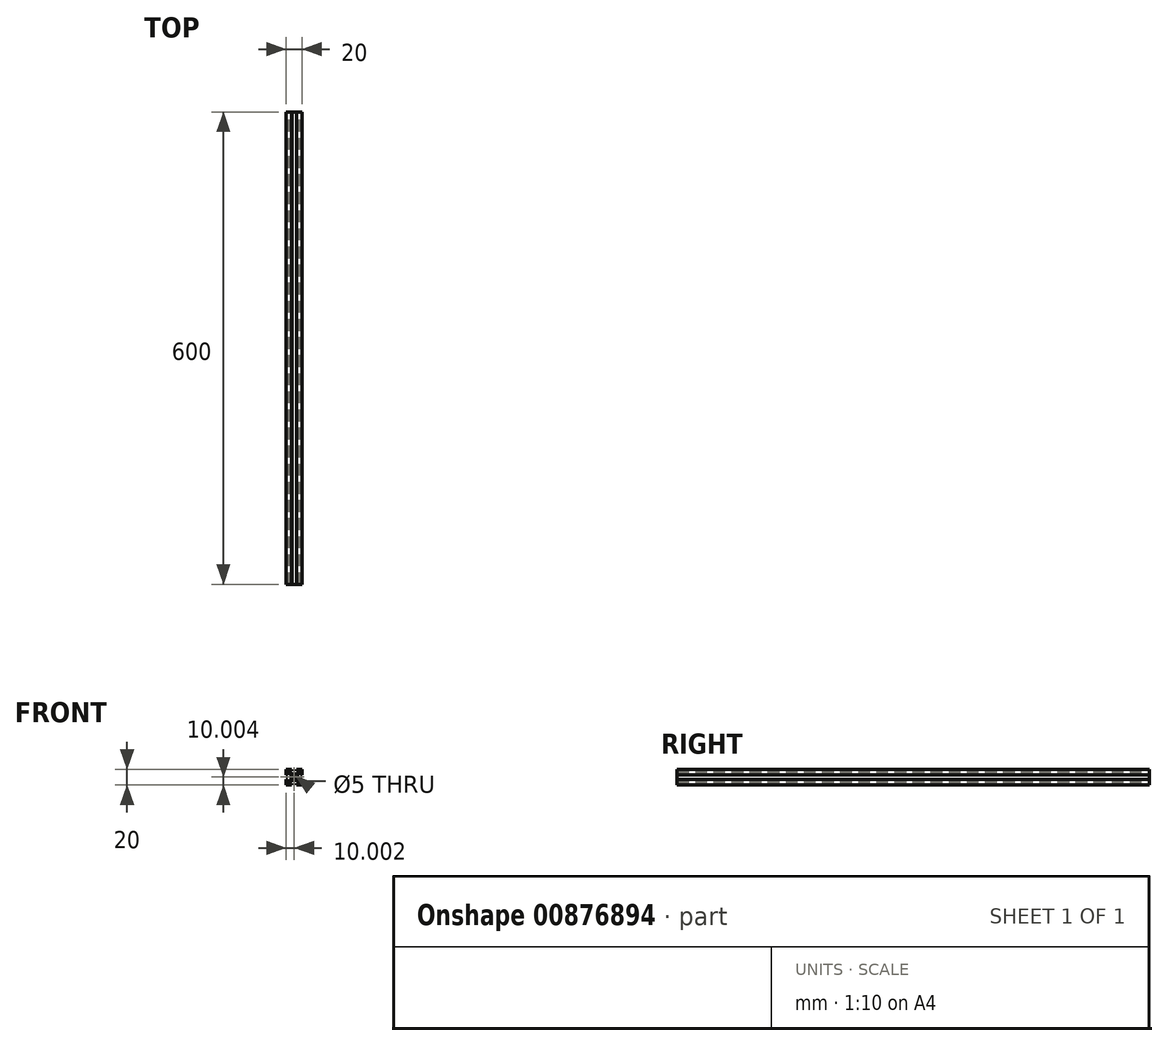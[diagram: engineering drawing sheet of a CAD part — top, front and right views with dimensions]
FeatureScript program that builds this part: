
annotation { "Feature Type Name" : "Feature", "Feature Type Description" : "" }
export const myFeature = defineFeature(function(context is Context, id is Id, definition is map)
    precondition{}
    {
        {
            var Q0;
            Q0=qCreatedBy(makeId("Front.planeOp"),FACE);
            var sketch = newSketch(context, id + "F0", { "sketchPlane" : qUnion([Q0])});
            skLineSegment(sketch, "E0.bottom", {"start": v(-32.56, 59.93) * mm, "end": v(-12.56, 59.93) * mm});
            skLineSegment(sketch, "E0.top", {"start": v(-32.56, 39.93) * mm, "end": v(-12.56, 39.93) * mm});
            skLineSegment(sketch, "E0.left", {"start": v(-32.56, 59.93) * mm, "end": v(-32.56, 39.93) * mm});
            skLineSegment(sketch, "E0.right", {"start": v(-12.56, 59.93) * mm, "end": v(-12.56, 39.93) * mm});
            skPoint(sketch, "E0.middle", {"position": v(-22.56, 49.93) * mm});
            skLineSegment(sketch, "E1", {"start": v(-14.36, 53.03) * mm, "end": v(-12.56, 53.03) * mm});
            skLineSegment(sketch, "E2.MirrorCS", {"start": v(-14.36, 46.83) * mm, "end": v(-12.56, 46.83) * mm});
            skLineSegment(sketch, "E3", {"start": v(-14.36, 53.03) * mm, "end": v(-14.36, 55.43) * mm});
            skLineSegment(sketch, "E4.MirrorCS", {"start": v(-14.36, 46.83) * mm, "end": v(-14.36, 44.43) * mm});
            skLineSegment(sketch, "E5", {"start": v(-14.36, 55.43) * mm, "end": v(-15.96, 55.43) * mm});
            skLineSegment(sketch, "E6.MirrorCS", {"start": v(-14.36, 44.43) * mm, "end": v(-15.96, 44.43) * mm});
            skCircle(sketch, "E7", {"center": v(-22.56, 49.93) * mm, "radius": 2.5 * mm});
            skLineSegment(sketch, "E8", {"start": v(-18.46, 52.93) * mm, "end": v(-18.46, 46.93) * mm});
            skLineSegment(sketch, "E9", {"start": v(-18.46, 52.93) * mm, "end": v(-15.96, 55.43) * mm});
            skLineSegment(sketch, "E10.MirrorCS", {"start": v(-18.46, 46.93) * mm, "end": v(-15.96, 44.43) * mm});
            skLineSegment(sketch, "E11.MirrorCS", {"start": v(-30.76, 53.03) * mm, "end": v(-32.56, 53.03) * mm});
            skLineSegment(sketch, "E12.MirrorCS", {"start": v(-30.76, 53.03) * mm, "end": v(-30.76, 55.43) * mm});
            skLineSegment(sketch, "E13.MirrorCS", {"start": v(-30.76, 55.43) * mm, "end": v(-29.16, 55.43) * mm});
            skLineSegment(sketch, "E14.MirrorCS", {"start": v(-26.66, 52.93) * mm, "end": v(-29.16, 55.43) * mm});
            skLineSegment(sketch, "E15.MirrorCS", {"start": v(-26.66, 52.93) * mm, "end": v(-26.66, 46.93) * mm});
            skLineSegment(sketch, "E16.MirrorCS", {"start": v(-26.66, 46.93) * mm, "end": v(-29.16, 44.43) * mm});
            skLineSegment(sketch, "E17.MirrorCS", {"start": v(-30.76, 44.43) * mm, "end": v(-29.16, 44.43) * mm});
            skLineSegment(sketch, "E18.MirrorCS", {"start": v(-30.76, 46.83) * mm, "end": v(-30.76, 44.43) * mm});
            skLineSegment(sketch, "E19.MirrorCS", {"start": v(-30.76, 46.83) * mm, "end": v(-32.56, 46.83) * mm});
            skLineSegment(sketch, "E20", {"start": v(-25.66, 59.93) * mm, "end": v(-25.66, 58.13) * mm});
            skLineSegment(sketch, "E21", {"start": v(-25.66, 58.13) * mm, "end": v(-28.06, 58.13) * mm});
            skLineSegment(sketch, "E22", {"start": v(-28.06, 58.13) * mm, "end": v(-28.06, 56.53) * mm});
            skLineSegment(sketch, "E23", {"start": v(-25.56, 54.03) * mm, "end": v(-22.56, 54.03) * mm});
            skLineSegment(sketch, "E24.MirrorCS", {"start": v(-19.46, 59.93) * mm, "end": v(-19.46, 58.13) * mm});
            skLineSegment(sketch, "E25.MirrorCS", {"start": v(-19.46, 58.13) * mm, "end": v(-17.06, 58.13) * mm});
            skLineSegment(sketch, "E26.MirrorCS", {"start": v(-17.06, 58.13) * mm, "end": v(-17.06, 56.53) * mm});
            skLineSegment(sketch, "E27.MirrorCS", {"start": v(-19.56, 54.03) * mm, "end": v(-22.56, 54.03) * mm});
            skLineSegment(sketch, "E28", {"start": v(-17.06, 56.53) * mm, "end": v(-19.56, 54.03) * mm});
            skLineSegment(sketch, "E29", {"start": v(-28.06, 56.53) * mm, "end": v(-25.56, 54.03) * mm});
            skLineSegment(sketch, "E30.MirrorCS", {"start": v(-25.66, 39.93) * mm, "end": v(-25.66, 41.73) * mm});
            skLineSegment(sketch, "E31.MirrorCS", {"start": v(-25.66, 41.73) * mm, "end": v(-28.06, 41.73) * mm});
            skLineSegment(sketch, "E32.MirrorCS", {"start": v(-28.06, 41.73) * mm, "end": v(-28.06, 43.33) * mm});
            skLineSegment(sketch, "E33.MirrorCS", {"start": v(-28.06, 43.33) * mm, "end": v(-25.56, 45.83) * mm});
            skLineSegment(sketch, "E34.MirrorCS", {"start": v(-19.46, 39.93) * mm, "end": v(-19.46, 41.73) * mm});
            skLineSegment(sketch, "E35.MirrorCS", {"start": v(-19.46, 41.73) * mm, "end": v(-17.06, 41.73) * mm});
            skLineSegment(sketch, "E36.MirrorCS", {"start": v(-17.06, 41.73) * mm, "end": v(-17.06, 43.33) * mm});
            skLineSegment(sketch, "E37.MirrorCS", {"start": v(-17.06, 43.33) * mm, "end": v(-19.56, 45.83) * mm});
            skLineSegment(sketch, "E38.MirrorCS", {"start": v(-19.56, 45.83) * mm, "end": v(-22.56, 45.83) * mm});
            skLineSegment(sketch, "E39.MirrorCS", {"start": v(-25.56, 45.83) * mm, "end": v(-22.56, 45.83) * mm});
            skSolve(sketch);
        }
        {
            var Q0;
            {var subQ5=sQuery(id+"F0.wireOp",EDGE,"E1");Q0=makeQuery(id+"F0.imprint","IMPRINT",FACE,{"disambiguationData":[TD([[makeQuery(id+"F0.imprint","IMPRINT",EDGE,{"derivedFrom":subQ5}),1.0]])]});}
            extrude(context, id + "F1", {"entities" : qUnion([Q0]), "depth" : 600 * mm, "offsetDistance" : 25 * mm});
        }
    });
